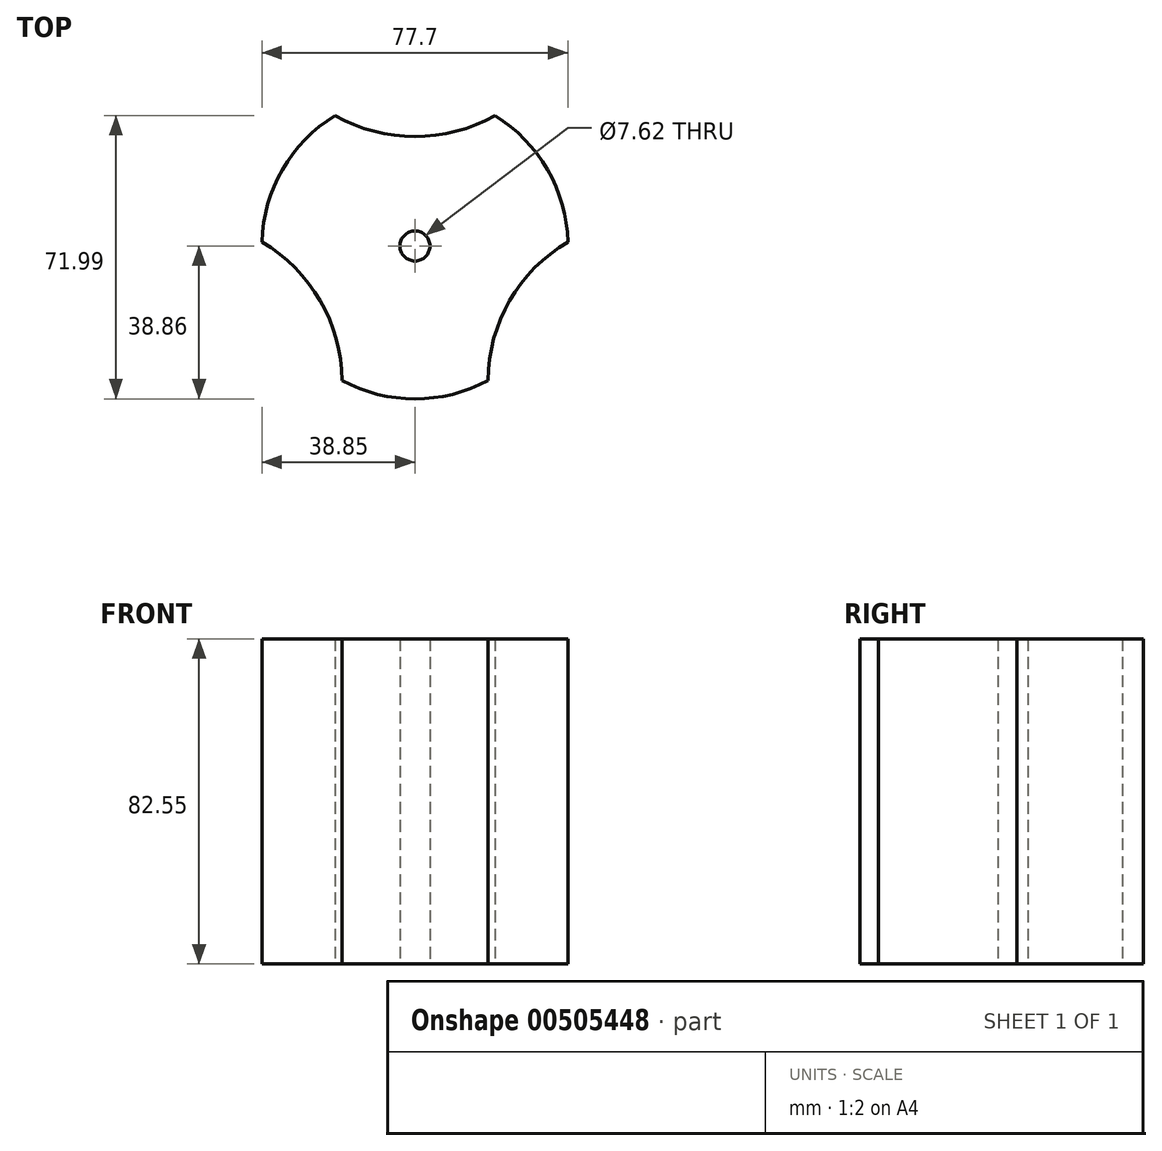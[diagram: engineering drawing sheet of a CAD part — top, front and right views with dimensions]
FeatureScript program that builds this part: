
annotation { "Feature Type Name" : "Feature", "Feature Type Description" : "" }
export const myFeature = defineFeature(function(context is Context, id is Id, definition is map)
    precondition{}
    {
        {
            var Q0;
            Q0=qCreatedBy(makeId("Top.planeOp"),FACE);
            var sketch = newSketch(context, id + "F0", { "sketchPlane" : qUnion([Q0])});
            skCircle(sketch, "E0", {"center": v(0, 0) * mm, "radius": 3.81 * mm});
            skArc(sketch, "E1", {"start": v(-20.3, 33.13) * mm, "mid": v(-33.66, 19.43) * mm, "end": v(-38.85, 1.02) * mm});
            skArc(sketch, "E2", {"start": v(-20.3, 33.13) * mm, "mid": v(0, 27.8) * mm, "end": v(20.3, 33.13) * mm});
            skArc(sketch, "E3.1.0", {"start": v(-18.54, -34.15) * mm, "mid": v(-24.07, -13.9) * mm, "end": v(-38.85, 1.02) * mm});
            skArc(sketch, "E3.2.0", {"start": v(38.85, 1.02) * mm, "mid": v(24.07, -13.9) * mm, "end": v(18.54, -34.15) * mm});
            skArc(sketch, "E4.trimOffspring", {"start": v(-18.54, -34.15) * mm, "mid": v(0, -38.86) * mm, "end": v(18.54, -34.15) * mm});
            skArc(sketch, "E5.trimOffspring", {"start": v(38.85, 1.02) * mm, "mid": v(33.66, 19.43) * mm, "end": v(20.3, 33.13) * mm});
            skArc(sketch, "E6", {"start": v(-28.78, 26.12) * mm, "mid": v(-24.38, 26.06) * mm, "end": v(-24.14, 30.45) * mm});
            skArc(sketch, "E7", {"start": v(-38.44, 5.68) * mm, "mid": v(-34.76, 8.08) * mm, "end": v(-37, 11.86) * mm});
            skPoint(sketch, "E8.center.orphan", {"position": v(-33.66, 19.43) * mm});
            skArc(sketch, "E9.1.0", {"start": v(-8.23, -37.98) * mm, "mid": v(-10.38, -34.14) * mm, "end": v(-14.3, -36.13) * mm});
            skArc(sketch, "E9.1.1", {"start": v(14.3, -36.13) * mm, "mid": v(10.38, -34.14) * mm, "end": v(8.23, -37.98) * mm});
            skArc(sketch, "E9.2.0", {"start": v(37, 11.86) * mm, "mid": v(34.76, 8.08) * mm, "end": v(38.44, 5.68) * mm});
            skArc(sketch, "E9.2.1", {"start": v(24.14, 30.45) * mm, "mid": v(24.38, 26.06) * mm, "end": v(28.78, 26.12) * mm});
            skSolve(sketch);
        }
        {
            var Q0;
            Q0 = qSketchRegion(id + "F0", true);
            extrude(context, id + "F1", {"entities" : qUnion([Q0]), "depth" : 82.55 * mm});
        }
    });
